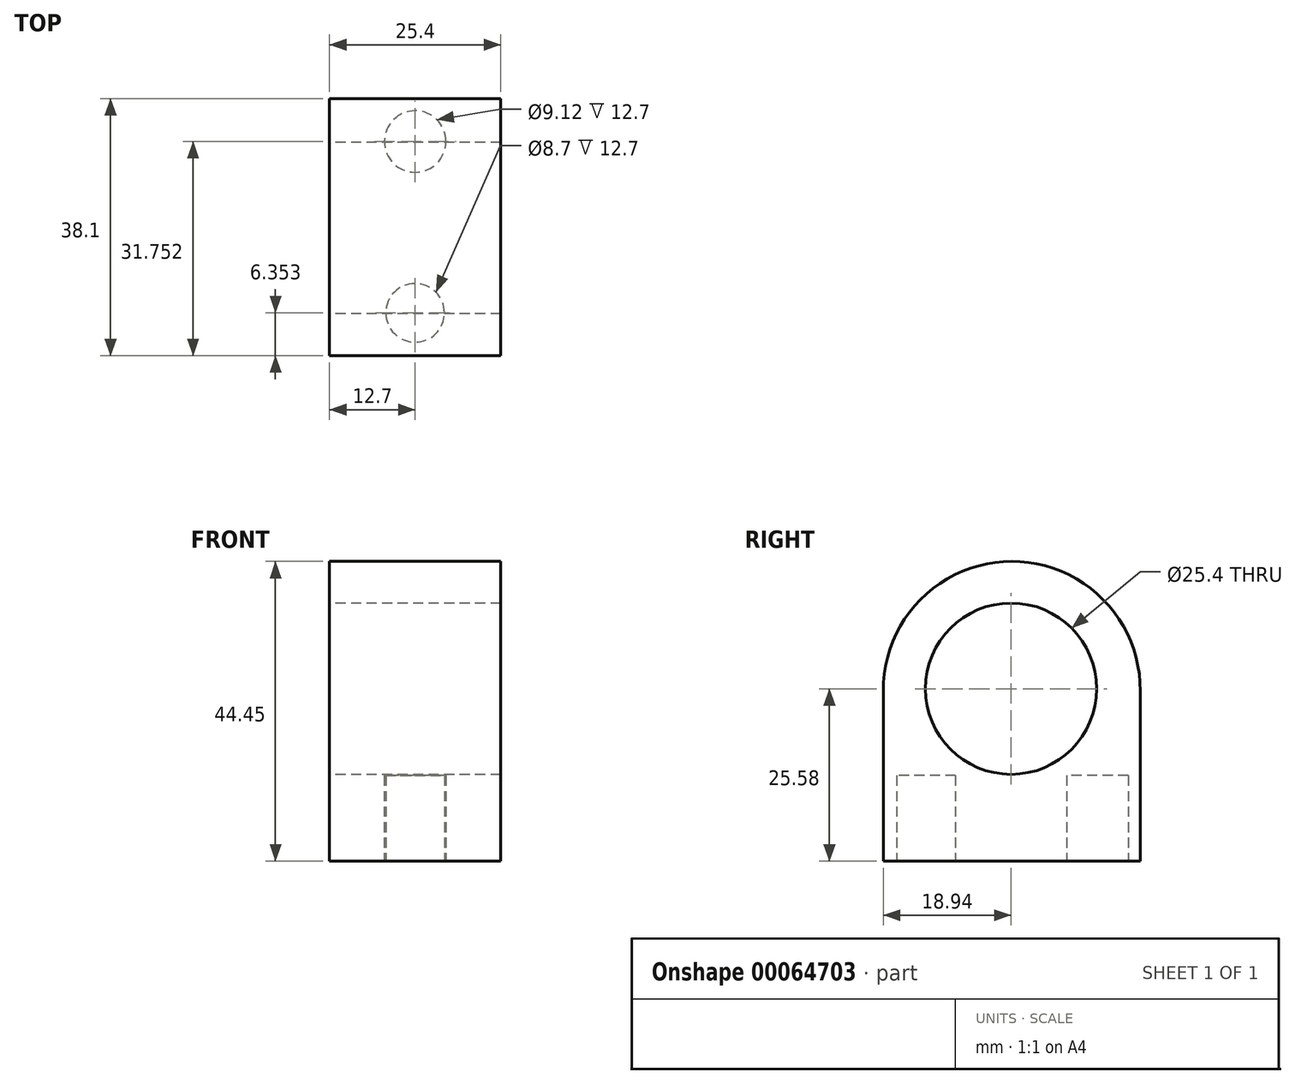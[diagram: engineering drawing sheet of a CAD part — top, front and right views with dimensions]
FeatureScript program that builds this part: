
annotation { "Feature Type Name" : "Feature", "Feature Type Description" : "" }
export const myFeature = defineFeature(function(context is Context, id is Id, definition is map)
    precondition{}
    {
        {
            var Q0;
            Q0=qCreatedBy(makeId("Right.planeOp"),FACE);
            var sketch = newSketch(context, id + "F0", { "sketchPlane" : qUnion([Q0])});
            skCircle(sketch, "E0", {"center": v(0, 0) * mm, "radius": 12.7 * mm});
            skArc(sketch, "E1", {"start": v(19.16, -0.36) * mm, "mid": v(0.11, 18.87) * mm, "end": v(-18.94, -0.36) * mm});
            skLineSegment(sketch, "E2", {"start": v(-18.94, 0) * mm, "end": v(-18.94, -25.58) * mm});
            skLineSegment(sketch, "E3", {"start": v(19.16, 0) * mm, "end": v(19.16, -25.58) * mm});
            skLineSegment(sketch, "E4", {"start": v(19.16, -25.58) * mm, "end": v(-18.94, -25.58) * mm});
            skSolve(sketch);
        }
        {
            var Q0;
            Q0 = qSketchRegion(id + "F0", true);
            extrude(context, id + "F1", {"entities" : qUnion([Q0]), "depth" : 25.4 * mm});
        }
        {
            var Q0;
            Q0=makeQuery(id+"F1.opExtrude","SWEPT_FACE",FACE,{"disambiguationData":[OSD([sQuery(id+"F0.wireOp",EDGE,"E4")])]});
            var sketch = newSketch(context, id + "F2", { "sketchPlane" : qUnion([Q0])});
            skCircle(sketch, "E5", {"center": v(12.7, 12.59) * mm, "radius": 4.35 * mm});
            skCircle(sketch, "E6", {"center": v(12.7, -12.81) * mm, "radius": 4.56 * mm});
            skSolve(sketch);
        }
        {
            var Q0;
            Q0 = qSketchRegion(id + "F2", true);
            extrude(context, id + "F3", {"entities" : qUnion([Q0]), "operationType" : NewBodyOperationType.REMOVE, "oppositeDirection" : true, "depth" : 12.7 * mm});
        }
    });
